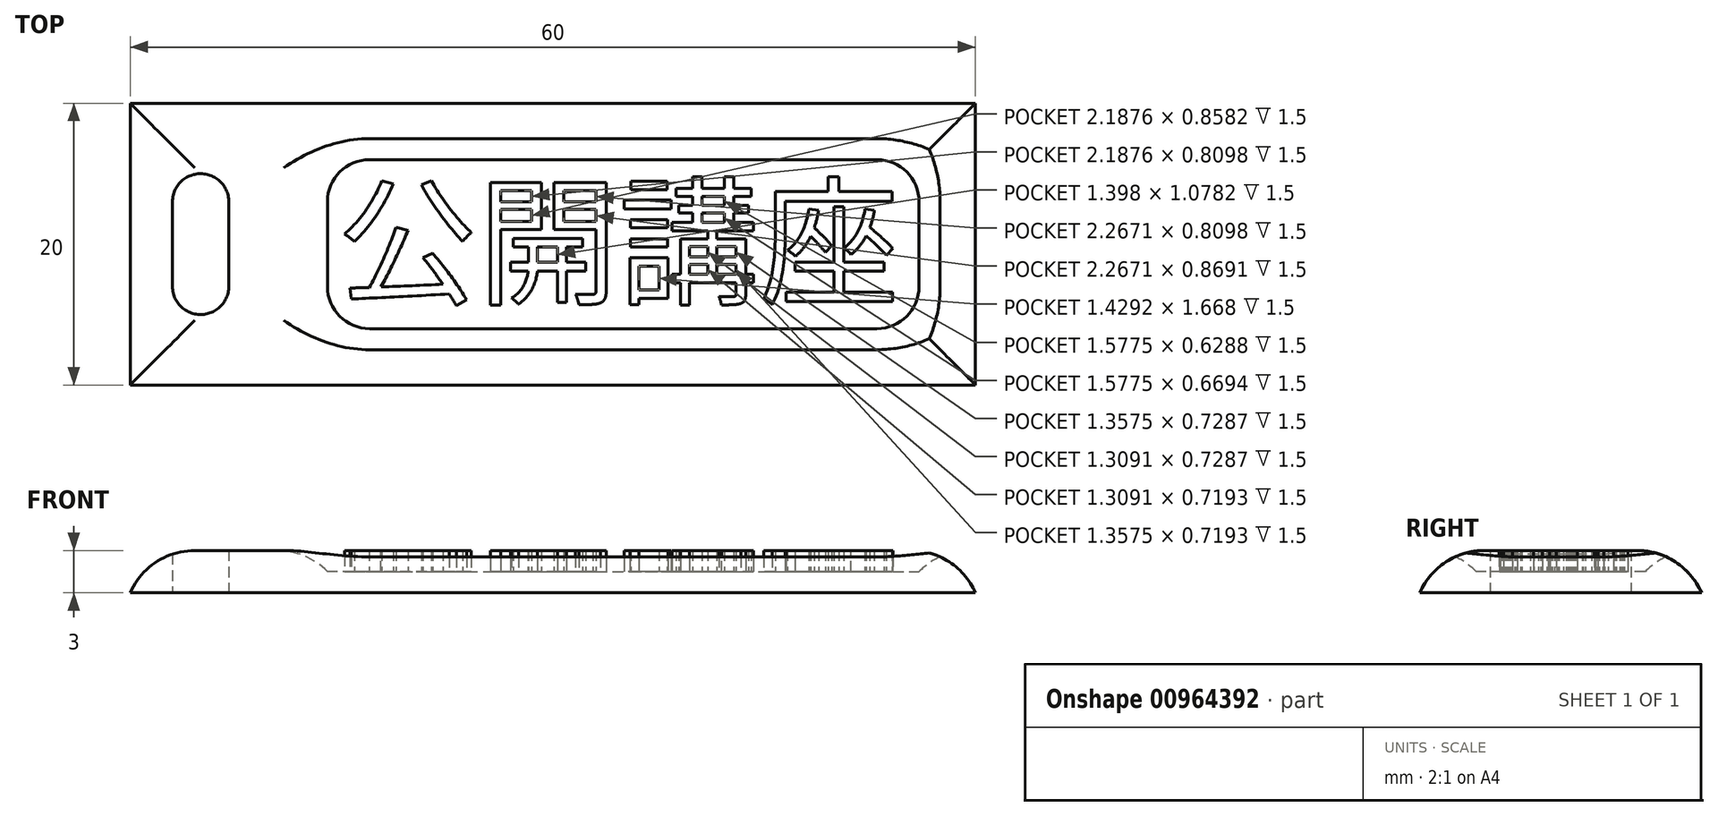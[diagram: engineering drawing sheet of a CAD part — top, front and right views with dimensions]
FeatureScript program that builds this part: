
annotation { "Feature Type Name" : "Feature", "Feature Type Description" : "" }
export const myFeature = defineFeature(function(context is Context, id is Id, definition is map)
    precondition{}
    {
        {
            var Q0;
            Q0=qCreatedBy(makeId("Top.planeOp"),FACE);
            var sketch = newSketch(context, id + "F0", { "sketchPlane" : qUnion([Q0])});
            skLineSegment(sketch, "E0.bottom", {"start": v(25, 10) * mm, "end": v(-25, 10) * mm});
            skLineSegment(sketch, "E0.top", {"start": v(25, -10) * mm, "end": v(-25, -10) * mm});
            skLineSegment(sketch, "E0.left", {"start": v(25, 10) * mm, "end": v(25, -10) * mm});
            skLineSegment(sketch, "E0.right", {"start": v(-25, 10) * mm, "end": v(-25, -10) * mm});
            skPoint(sketch, "E0.middle", {"position": v(0, 0) * mm});
            skLineSegment(sketch, "E1.bottom", {"start": v(-25, 10) * mm, "end": v(-35, 10) * mm});
            skLineSegment(sketch, "E1.top", {"start": v(-25, -10) * mm, "end": v(-35, -10) * mm});
            skLineSegment(sketch, "E1.right", {"start": v(-35, 10) * mm, "end": v(-35, -10) * mm});
            skPoint(sketch, "E1.middle", {"position": v(-30, 0) * mm});
            skLineSegment(sketch, "E2.bottom", {"start": v(-30, 5) * mm, "end": v(-30, 5) * mm});
            skLineSegment(sketch, "E2.top", {"start": v(-30, -5) * mm, "end": v(-30, -5) * mm});
            skLineSegment(sketch, "E2.left", {"start": v(-28, 3) * mm, "end": v(-28, -3) * mm});
            skLineSegment(sketch, "E2.right", {"start": v(-32, 3) * mm, "end": v(-32, -3) * mm});
            skPoint(sketch, "E3.visualSharp", {"position": v(-32, 5) * mm});
            skArc(sketch, "E3.filletArc", {"start": v(-30, 5) * mm, "mid": v(-31.41, 4.41) * mm, "end": v(-32, 3) * mm});
            skPoint(sketch, "E4.visualSharp", {"position": v(-28, 5) * mm});
            skArc(sketch, "E4.filletArc", {"start": v(-28, 3) * mm, "mid": v(-28.59, 4.41) * mm, "end": v(-30, 5) * mm});
            skPoint(sketch, "E5.visualSharp", {"position": v(-32, -5) * mm});
            skArc(sketch, "E5.filletArc", {"start": v(-32, -3) * mm, "mid": v(-31.41, -4.41) * mm, "end": v(-30, -5) * mm});
            skPoint(sketch, "E6.visualSharp", {"position": v(-28, -5) * mm});
            skArc(sketch, "E6.filletArc", {"start": v(-30, -5) * mm, "mid": v(-28.59, -4.41) * mm, "end": v(-28, -3) * mm});
            skSolve(sketch);
        }
        {
            var Q0;
            Q0=qSketchRegion(id+"F0",true);
            extrude(context, id + "F1", {"entities" : qUnion([Q0]), "depth" : 3 * mm, "offsetDistance" : 25 * mm});
        }
        {
            var Q0;
            Q0=qCreatedBy(makeId("Top.planeOp"),FACE);
            var sketch = newSketch(context, id + "F2", { "sketchPlane" : qUnion([Q0])});
            skLineSegment(sketch, "E7.bottom", {"start": v(-18, 6) * mm, "end": v(18, 6) * mm});
            skLineSegment(sketch, "E7.top", {"start": v(-18, -6) * mm, "end": v(18, -6) * mm});
            skLineSegment(sketch, "E7.left", {"start": v(-21, 3) * mm, "end": v(-21, -3) * mm});
            skLineSegment(sketch, "E7.right", {"start": v(21, 3) * mm, "end": v(21, -3) * mm});
            skPoint(sketch, "E7.middle", {"position": v(0, 0) * mm});
            skPoint(sketch, "E8.visualSharp", {"position": v(-21, 6) * mm});
            skArc(sketch, "E8.filletArc", {"start": v(-18, 6) * mm, "mid": v(-20.12, 5.12) * mm, "end": v(-21, 3) * mm});
            skPoint(sketch, "E9.visualSharp", {"position": v(-21, -6) * mm});
            skArc(sketch, "E9.filletArc", {"start": v(-21, -3) * mm, "mid": v(-20.12, -5.12) * mm, "end": v(-18, -6) * mm});
            skPoint(sketch, "E10.visualSharp", {"position": v(21, 6) * mm});
            skArc(sketch, "E10.filletArc", {"start": v(21, 3) * mm, "mid": v(20.12, 5.12) * mm, "end": v(18, 6) * mm});
            skPoint(sketch, "E11.visualSharp", {"position": v(21, -6) * mm});
            skArc(sketch, "E11.filletArc", {"start": v(18, -6) * mm, "mid": v(20.12, -5.12) * mm, "end": v(21, -3) * mm});
            skSolve(sketch);
        }
        {
            var Q0;
            Q0=qSketchRegion(id+"F2",true);
            extrude(context, id + "F3", {"entities" : qUnion([Q0]), "depth" : 3 * mm, "offsetDistance" : 25 * mm});
        }
        {
            var Q0;
            Q0=makeQuery(id+"F3.opExtrude","SWEPT_BODY",BODY,{"disambiguationData":[OSD([sQuery(id+"F2.wireOp",EDGE,"E7.bottom"),sQuery(id+"F2.wireOp",EDGE,"E7.top"),sQuery(id+"F2.wireOp",EDGE,"E7.left"),sQuery(id+"F2.wireOp",EDGE,"E7.right"),sQuery(id+"F2.wireOp",EDGE,"E8.filletArc"),sQuery(id+"F2.wireOp",EDGE,"E9.filletArc"),sQuery(id+"F2.wireOp",EDGE,"E10.filletArc"),sQuery(id+"F2.wireOp",EDGE,"E11.filletArc")])]});
            transform(context, id + "F4", {"entities" : qUnion([Q0]), "transformType" : TransformType.TRANSLATION_3D, "dx" : 0 * mm, "dy" : 0 * mm, "dz" : 1.5 * mm, "makeCopy" : false});
        }
        {
            var Q0;
            Q0=makeQuery(id+"F3.opExtrude","SWEPT_BODY",BODY,{"disambiguationData":[OSD([sQuery(id+"F2.wireOp",EDGE,"E7.bottom"),sQuery(id+"F2.wireOp",EDGE,"E7.top"),sQuery(id+"F2.wireOp",EDGE,"E7.left"),sQuery(id+"F2.wireOp",EDGE,"E7.right"),sQuery(id+"F2.wireOp",EDGE,"E8.filletArc"),sQuery(id+"F2.wireOp",EDGE,"E9.filletArc"),sQuery(id+"F2.wireOp",EDGE,"E10.filletArc"),sQuery(id+"F2.wireOp",EDGE,"E11.filletArc")])]});
            var Q1;
            Q1=makeQuery(id+"F1.opExtrude","SWEPT_BODY",BODY,{"disambiguationData":[OSD([sQuery(id+"F0.wireOp",EDGE,"E0.bottom"),sQuery(id+"F0.wireOp",EDGE,"E0.top"),sQuery(id+"F0.wireOp",EDGE,"E0.left"),sQuery(id+"F0.wireOp",EDGE,"E1.bottom"),sQuery(id+"F0.wireOp",EDGE,"E1.top"),sQuery(id+"F0.wireOp",EDGE,"E1.right"),sQuery(id+"F0.wireOp",EDGE,"E2.left"),sQuery(id+"F0.wireOp",EDGE,"E2.right"),sQuery(id+"F0.wireOp",EDGE,"E3.filletArc"),sQuery(id+"F0.wireOp",EDGE,"E4.filletArc"),sQuery(id+"F0.wireOp",EDGE,"E5.filletArc"),sQuery(id+"F0.wireOp",EDGE,"E6.filletArc")])]});
            booleanBodies(context, id + "F5", {"operationType" : BooleanOperationType.SUBTRACTION, "tools" : qUnion([Q0]), "targets" : qUnion([Q1])});
        }
        {
            var Q0;
            Q0=qCreatedBy(makeId("Top.planeOp"),FACE);
            var sketch = newSketch(context, id + "F6", { "sketchPlane" : qUnion([Q0])});
            skText(sketch, "E12", { "text": "公開講座", "fontName": "NotoSansCJKjp-Regular.otf"});
            const initialGuessF6  = {"E12": [-0.02032, -0.00356, 1, 0, 0.00719]};
            skSetInitialGuess(sketch, initialGuessF6);
            skSolve(sketch);
        }
        {
            var Q0;
            Q0 = qSketchRegion(id + "F6", true);
            extrude(context, id + "F7", {"entities" : qUnion([Q0]), "operationType" : NewBodyOperationType.ADD, "depth" : 3 * mm, "offsetDistance" : 25 * mm});
        }
        {
            var Q0;
            Q0=makeQuery(id+"F1.opExtrude","CAP_EDGE",EDGE,{"disambiguationData":[OSD([sQuery(id+"F0.wireOp",EDGE,"E0.bottom"),sQuery(id+"F0.wireOp",EDGE,"E1.bottom")])],"isStart":false});
            var Q1;
            Q1=makeQuery(id+"F1.opExtrude","CAP_EDGE",EDGE,{"disambiguationData":[OSD([sQuery(id+"F0.wireOp",EDGE,"E1.right")])],"isStart":false});
            var Q2;
            Q2=makeQuery(id+"F1.opExtrude","CAP_EDGE",EDGE,{"disambiguationData":[OSD([sQuery(id+"F0.wireOp",EDGE,"E0.top"),sQuery(id+"F0.wireOp",EDGE,"E1.top")])],"isStart":false});
            var Q3;
            Q3=makeQuery(id+"F1.opExtrude","CAP_EDGE",EDGE,{"disambiguationData":[OSD([sQuery(id+"F0.wireOp",EDGE,"E0.left")])],"isStart":false});
            var Q4;
            Q4=makeQuery(id+"F5.opBoolean","INTERSECT",EDGE,{"derivedFrom":[makeQuery(id+"F1.opExtrude","CAP_FACE",FACE,{"disambiguationData":[OSD([sQuery(id+"F0.wireOp",EDGE,"E0.bottom"),sQuery(id+"F0.wireOp",EDGE,"E0.top"),sQuery(id+"F0.wireOp",EDGE,"E0.left"),sQuery(id+"F0.wireOp",EDGE,"E1.bottom"),sQuery(id+"F0.wireOp",EDGE,"E1.top"),sQuery(id+"F0.wireOp",EDGE,"E1.right"),sQuery(id+"F0.wireOp",EDGE,"E2.left"),sQuery(id+"F0.wireOp",EDGE,"E2.right"),sQuery(id+"F0.wireOp",EDGE,"E3.filletArc"),sQuery(id+"F0.wireOp",EDGE,"E4.filletArc"),sQuery(id+"F0.wireOp",EDGE,"E5.filletArc"),sQuery(id+"F0.wireOp",EDGE,"E6.filletArc")])],"isStart":false}),makeQuery(id+"F3.opExtrude","SWEPT_FACE",FACE,{"disambiguationData":[OSD([sQuery(id+"F2.wireOp",EDGE,"E7.top")])]})]});
            fillet(context, id + "F8", {"entities" : qUnion([Q0, Q1, Q2, Q3, Q4]), "radius" : 5 * mm, "tangentPropagation" : true, "allowEdgeOverflow" : false});
        }
    });
